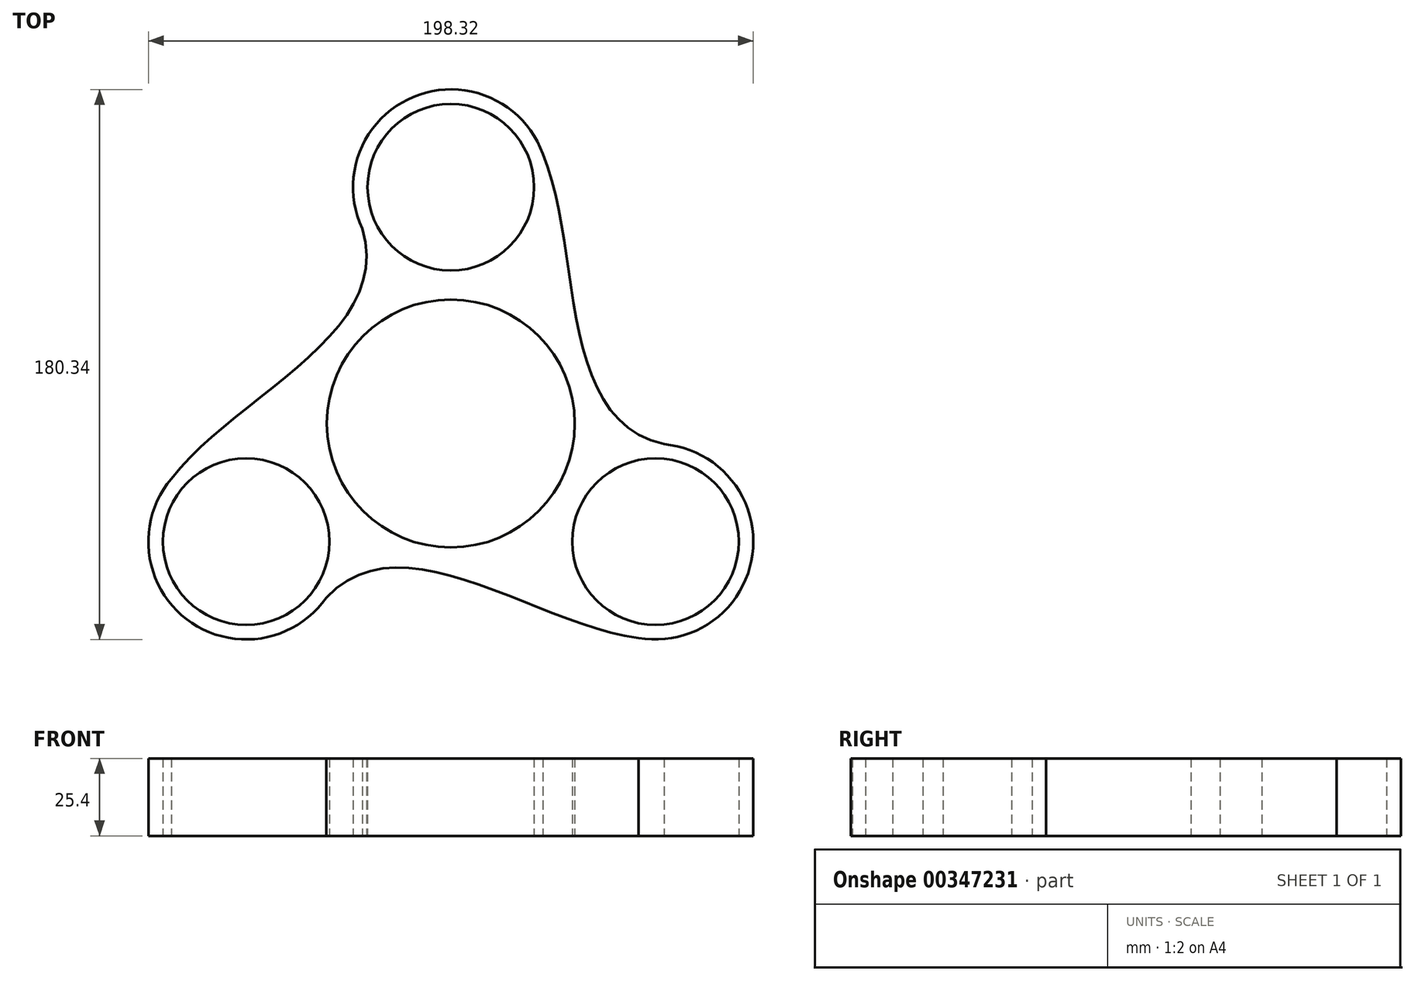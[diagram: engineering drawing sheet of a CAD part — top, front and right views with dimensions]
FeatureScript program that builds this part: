
annotation { "Feature Type Name" : "Feature", "Feature Type Description" : "" }
export const myFeature = defineFeature(function(context is Context, id is Id, definition is map)
    precondition{}
    {
        {
            var Q0;
            Q0=qCreatedBy(makeId("Top.planeOp"),FACE);
            var sketch = newSketch(context, id + "F0", { "sketchPlane" : qUnion([Q0])});
            skCircle(sketch, "E0", {"center": v(0.88, 0.46) * mm, "radius": 40.64 * mm});
            skCircle(sketch, "E1", {"center": v(-66.21, -38.27) * mm, "radius": 27.3 * mm});
            skCircle(sketch, "E2", {"center": v(67.97, -38.27) * mm, "radius": 27.3 * mm});
            skCircle(sketch, "E3", {"center": v(0.88, 77.93) * mm, "radius": 27.3 * mm});
            skCircle(sketch, "E4", {"center": v(-66.21, -38.27) * mm, "radius": 32.07 * mm});
            skCircle(sketch, "E5", {"center": v(0.88, 77.93) * mm, "radius": 32.07 * mm});
            skCircle(sketch, "E6", {"center": v(67.97, -38.27) * mm, "radius": 32.07 * mm});
            skFitSpline(sketch, "E7", {"points": [v(-28.2, 64.4) * mm, v(-90.77, -17.65) * mm], "startDerivative": vector(32.24, -104.89) * mm, "endDerivative": vector(-62.57, -82.06) * mm});
            skFitSpline(sketch, "E8", {"points": [v(70.8, -6.33) * mm, v(31.02, 88.9) * mm], "startDerivative": vector(-106.96, 24.52) * mm, "endDerivative": vector(-39.78, 95.22) * mm});
            skFitSpline(sketch, "E9", {"points": [v(-39.96, -56.69) * mm, v(62.39, -69.85) * mm], "startDerivative": vector(74.72, 80.37) * mm, "endDerivative": vector(102.35, -13.16) * mm});
            skSolve(sketch);
        }
        {
            var Q0;
            Q0=qSketchRegion(id+"F0",true);
            extrude(context, id + "F1", {"entities" : qUnion([Q0]), "endBound" : BoundingType.SYMMETRIC, "depth" : 25.4 * mm});
        }
    });
